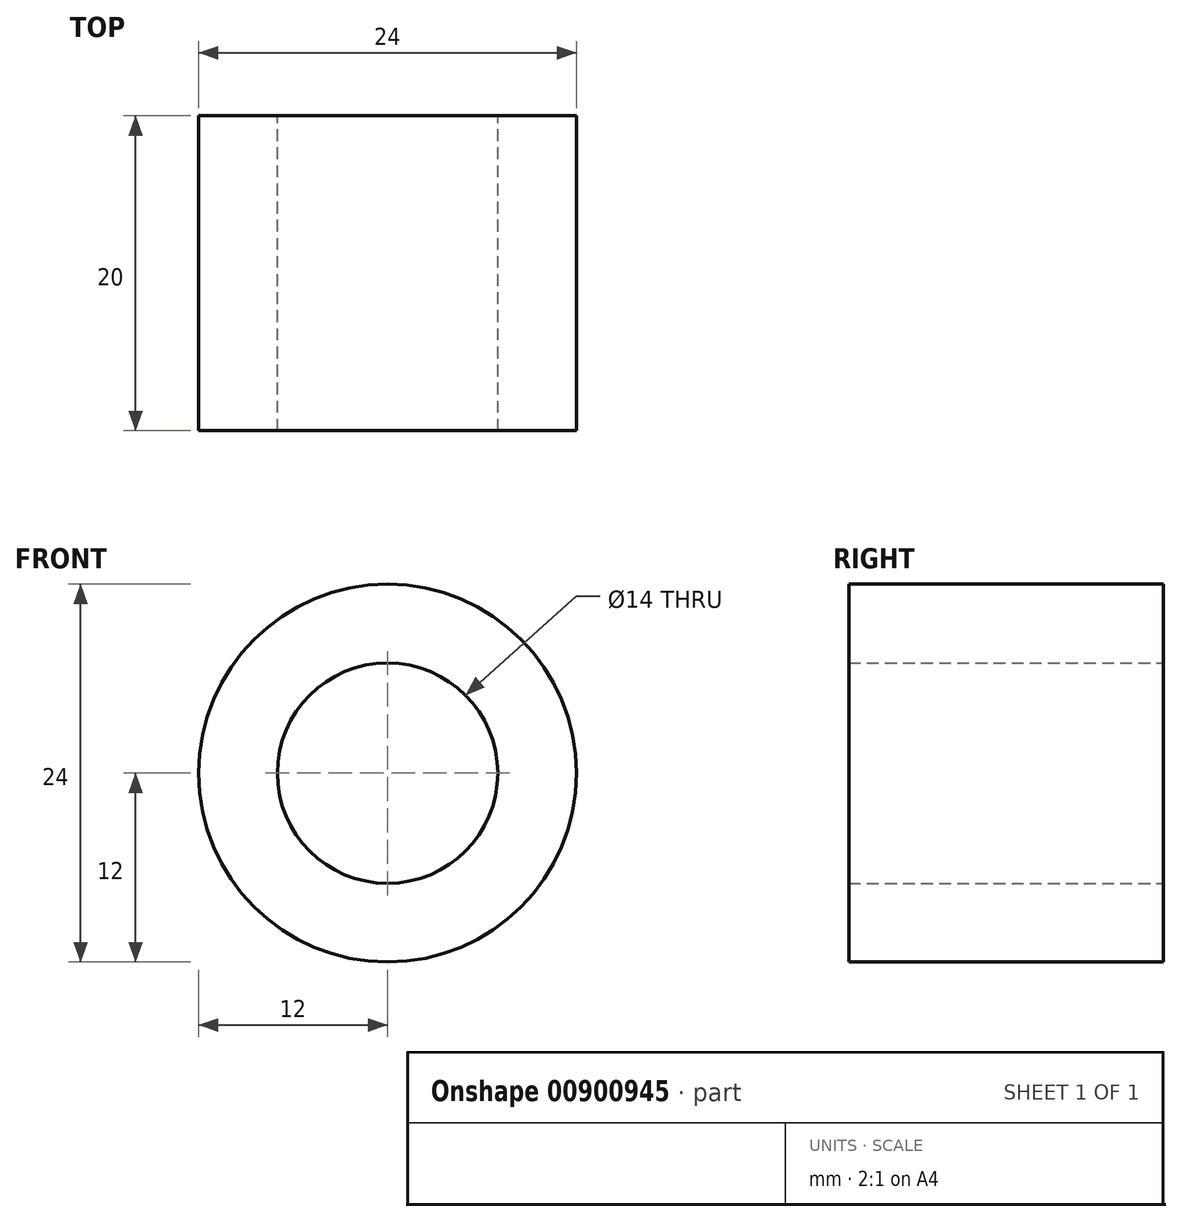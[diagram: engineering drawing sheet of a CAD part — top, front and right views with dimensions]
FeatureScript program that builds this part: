
annotation { "Feature Type Name" : "Feature", "Feature Type Description" : "" }
export const myFeature = defineFeature(function(context is Context, id is Id, definition is map)
    precondition{}
    {
        {
            var Q0;
            Q0=qCreatedBy(makeId("Front.planeOp"),FACE);
            var sketch = newSketch(context, id + "F0", { "sketchPlane" : qUnion([Q0])});
            skCircle(sketch, "E0", {"center": v(0, 0) * mm, "radius": 7 * mm});
            skCircle(sketch, "E1.0", {"center": v(0, 0) * mm, "radius": 12 * mm});
            skSolve(sketch);
        }
        {
            var Q0;
            Q0=makeQuery(id+"F0.imprint","IMPRINT",FACE,{"disambiguationData":[TD([[makeQuery(id+"F0.imprint","IMPRINT",EDGE,{"derivedFrom":sQuery(id+"F0.wireOp",EDGE,"E0")}),-1.0]])]});
            extrude(context, id + "F1", {"entities" : qUnion([Q0]), "depth" : 20 * mm, "offsetDistance" : 25 * mm});
        }
    });
